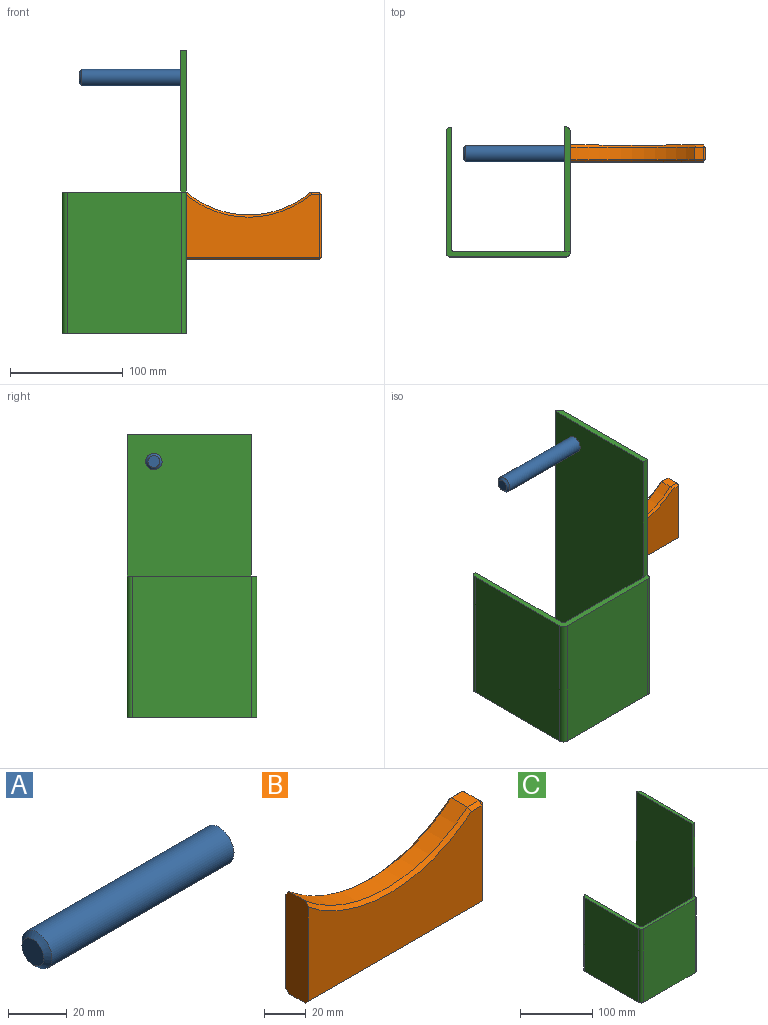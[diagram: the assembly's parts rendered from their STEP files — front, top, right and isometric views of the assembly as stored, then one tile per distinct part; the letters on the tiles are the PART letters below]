
ASSEMBLY  parts=3 mates=2
PART A: 4 faces, bbox 90x14.5x14.5 mm
  f0: cylinder r=7.25mm len=88mm, axis (-1,0,0), area 4008.7mm2, adj f1,f3
  f1: plane 14.5x14.5mm, normal (1,0,0), area 165.1mm2, adj f0
  f2: plane 10.5x10.5mm, normal (-1,0,0), area 86.6mm2, adj f3
  f3: cone r=7.25mm half-angle=45deg, axis (1,0,0), area 111.1mm2, adj f0,f2
PART B: 21 faces, bbox 121.3x15x60 mm
  f0: plane 11x8mm, normal (0,0,1), area 88mm2, adj f6,f10,f16,f19
  f1: plane 118x56mm, normal (0,-1,0), area 5069.1mm2, adj f5,f13,f17,f19,f20
  f2: plane 118x56mm, normal (0,1,0), area 5069.1mm2, adj f5,f7,f8,f10,f11
  f3: plane 118x11mm, normal (0,0,-1), area 1298mm2, adj f5,f7,f12,f13
  f4: plane 56x11mm, normal (1,0,0), area 616mm2, adj f11,f12,f16,f17
  f5: plane 60x15mm, normal (-1,0,0), area 890.8mm2, adj f1,f2,f3,f6,f7,f8,f13,f20
  f6: cylinder r=85mm len=110mm, axis (0,-1,0), area 1316mm2, adj f0,f5,f8,f20
  f7: plane 118x2mm, normal (0,0.71,-0.71), area 333.8mm2, adj f2,f3,f5,f9
  f8: cone r=87mm half-angle=45deg, axis (0,1,0), area 338.9mm2, adj f2,f5,f6,f10
  f9: plane 2x2mm, normal (0.58,0.58,-0.58), area 3.5mm2, adj f7,f11,f12
  f10: plane 8.01x2.01mm, normal (0,0.71,0.71), area 21.6mm2, adj f0,f2,f8,f14
  f11: plane 56x2mm, normal (0.71,0.71,0), area 158.4mm2, adj f2,f4,f9,f14
  f12: plane 11x2mm, normal (0.71,0,-0.71), area 31.1mm2, adj f3,f4,f9,f15
  f13: plane 118x2mm, normal (0,-0.71,-0.71), area 333.8mm2, adj f1,f3,f5,f15
  f14: plane 2x2mm, normal (0.58,0.58,0.58), area 3.5mm2, adj f10,f11,f16
  f15: plane 2x2mm, normal (0.58,-0.58,-0.58), area 3.5mm2, adj f12,f13,f17
  f16: plane 11x2mm, normal (0.71,0,0.71), area 31.1mm2, adj f0,f4,f14,f18
  f17: plane 56x2mm, normal (0.71,-0.71,0), area 158.4mm2, adj f1,f4,f15,f18
  f18: plane 2x2mm, normal (0.58,-0.58,0.58), area 3.5mm2, adj f16,f17,f19
  f19: plane 8.01x2.01mm, normal (0,-0.71,0.71), area 21.6mm2, adj f0,f1,f18,f20
  f20: cone r=85mm half-angle=45deg, axis (0,-1,0), area 338.9mm2, adj f1,f5,f6,f19
PART C: 18 faces, bbox 110x115x250 mm
  f0: plane 250x110mm, normal (-1,0,0), area 27312.5mm2, adj f3,f7,f9,f10,f15,f17
  f1: plane 125x0.5mm, normal (0,1,0), area 62.5mm2, adj f4,f9,f10,f14
  f2: plane 125x101mm, normal (0,-1,0), area 12625mm2, adj f9,f10,f11,f12
  f3: plane 110x5mm, normal (0,0,1), area 545.7mm2, adj f0,f6,f7,f13,f17
  f4: plane 125x108.5mm, normal (1,0,0), area 13562.5mm2, adj f1,f9,f10,f16
  f5: plane 125x106mm, normal (-1,0,0), area 13250mm2, adj f9,f10,f11,f14
  f6: plane 250x106mm, normal (1,0,0), area 26437.5mm2, adj f3,f9,f10,f12,f13,f17
  f7: plane 250x0.5mm, normal (0,1,0), area 125mm2, adj f0,f3,f9,f13
  f8: plane 125x97mm, normal (0,1,0), area 12125mm2, adj f9,f10,f15,f16
  f9: plane 115x110mm, normal (0,0,-1), area 1633.6mm2, adj f0,f1,f2,f4,f5,f6,f7,f8
  f10: plane 115x110mm, normal (0,0,1), area 1087.9mm2, adj f0,f1,f2,f4,f5,f6,f8,f11
  f11: cylinder r=4.5mm len=125mm, axis (0,0,1), area 883.6mm2, adj f2,f5,f9,f10
  f12: cylinder r=4.5mm len=125mm, axis (0,0,-1), area 883.6mm2, adj f2,f6,f9,f10
  f13: cylinder r=4.5mm len=250mm, axis (0,0,1), area 1767.1mm2, adj f3,f6,f7,f9
  f14: cylinder r=4.5mm len=125mm, axis (0,0,-1), area 883.6mm2, adj f1,f5,f9,f10
  f15: cylinder r=1.5mm len=125mm, axis (0,0,-1), area 294.5mm2, adj f0,f8,f9,f10
  f16: cylinder r=1.5mm len=125mm, axis (0,0,1), area 294.5mm2, adj f4,f8,f9,f10
  f17: plane 125x5mm, normal (0,-1,0), area 625mm2, adj f0,f3,f6,f10
PLACE A t=(-327.91,298.16,19.52)mm
PLACE B t=(-232.91,90.92,67.43)mm
PLACE C t=(-38.08,-48.47,-34.61)mm
MATE fastened B.f5 <-> C.f6  axis (-1,0,0) through (-232.91,-71.84,60.24)mm
MATE fastened A.f0 <-> C.f0  axis (1,0,0) through (-237.91,-72.22,191.64)mm
